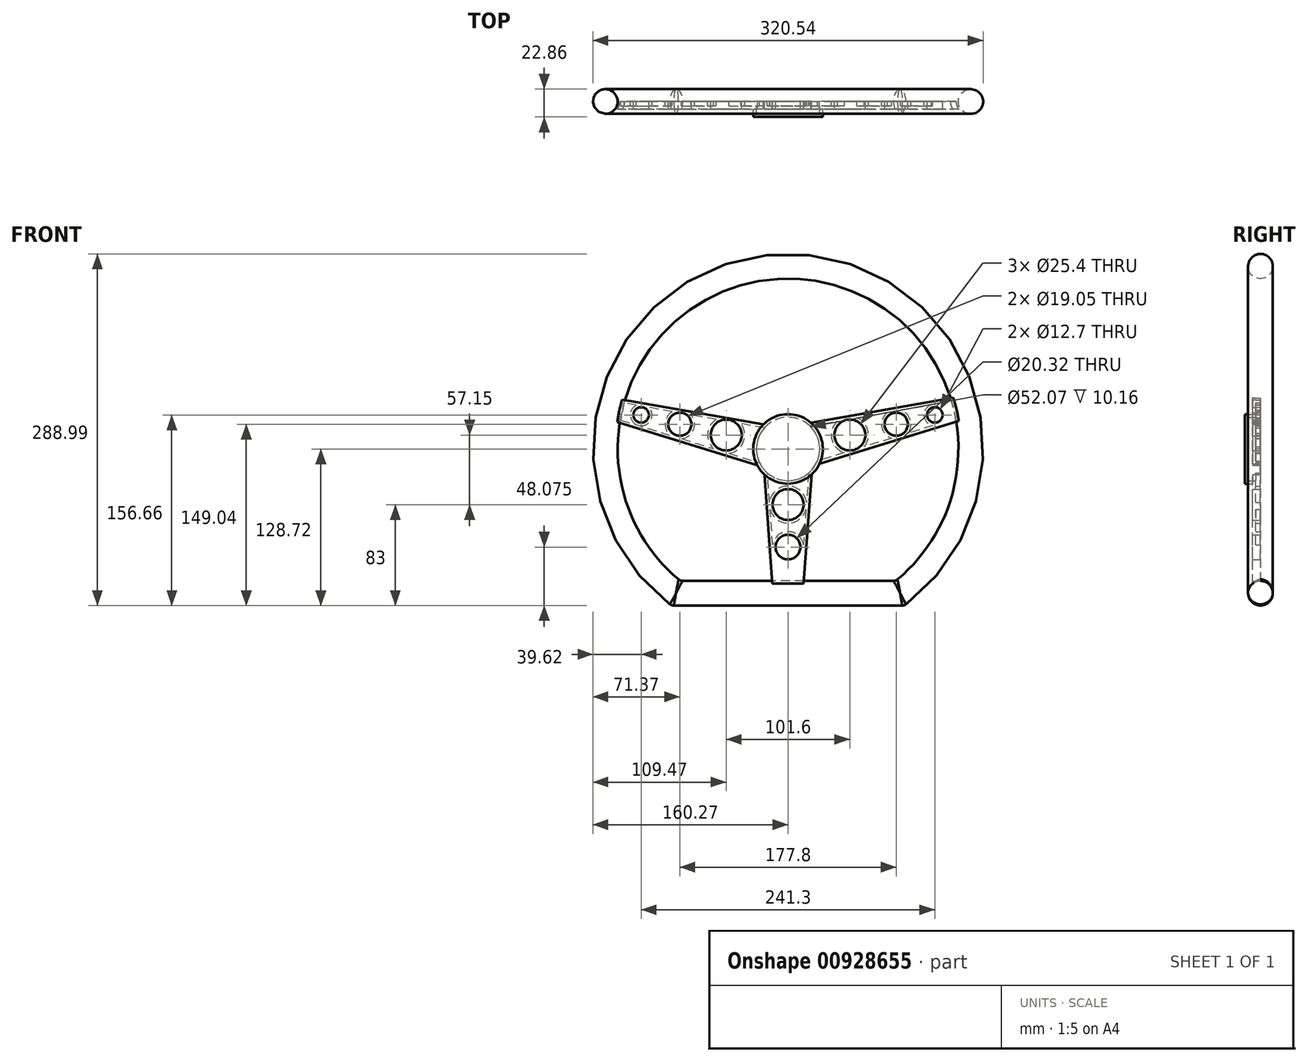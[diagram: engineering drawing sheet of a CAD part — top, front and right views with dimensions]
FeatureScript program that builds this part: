
annotation { "Feature Type Name" : "Feature", "Feature Type Description" : "" }
export const myFeature = defineFeature(function(context is Context, id is Id, definition is map)
    precondition{}
    {
        {
            var Q0;
            Q0=qCreatedBy(makeId("Front.planeOp"),FACE);
            var sketch = newSketch(context, id + "F0", { "sketchPlane" : qUnion([Q0])});
            skArc(sketch, "E0", {"start": v(92.08, -118.56) * mm, "mid": v(0, 150.11) * mm, "end": v(-92.08, -118.56) * mm});
            skLineSegment(sketch, "E1", {"start": v(-92.08, -118.56) * mm, "end": v(92.08, -118.56) * mm});
            skSolve(sketch);
        }
        {
            var Q0;
            Q0=qCreatedBy(makeId("Right.planeOp"),FACE);
            var sketch = newSketch(context, id + "F1", { "sketchPlane" : qUnion([Q0])});
            skCircle(sketch, "E2", {"center": v(0, 150.11) * mm, "radius": 10.16 * mm});
            skSolve(sketch);
        }
        {
            var Q0;
            Q0=makeQuery(id+"F1.imprint","IMPRINT",FACE,{"disambiguationData":[TD([[makeQuery(id+"F1.imprint","IMPRINT",EDGE,{"derivedFrom":sQuery(id+"F1.wireOp",EDGE,"E2")}),1.0]])]});
            var Q1;
            Q1=sQuery(id+"F0.wireOp",EDGE,"E0");
            var Q2;
            Q2=sQuery(id+"F0.wireOp",EDGE,"E1");
            sweep(context, id + "F2", {"profiles" : qUnion([Q0]), "path" : qUnion([Q1, Q2])});
        }
        {
            var Q0;
            Q0=makeQuery(id+"F2.opSweep","MID_CAP_EDGE",EDGE,{"disambiguationData":[OSD([sQuery(id+"F0.wireOp",VERTEX,"E1.end"),sQuery(id+"F1.wireOp",EDGE,"E2")]),OD(0.0)],"capPos":0.0});
            fillet(context, id + "F3", {"entities" : qUnion([Q0]), "radius" : 5.08 * mm, "tangentPropagation" : true, "allowEdgeOverflow" : false});
        }
        {
            var Q0;
            Q0=makeQuery(id+"F2.opSweep","MID_CAP_EDGE",EDGE,{"disambiguationData":[OSD([sQuery(id+"F0.wireOp",VERTEX,"E1.start"),sQuery(id+"F1.wireOp",EDGE,"E2")]),OD(0.0)],"capPos":1.0});
            fillet(context, id + "F4", {"entities" : qUnion([Q0]), "radius" : 5.08 * mm, "tangentPropagation" : true, "allowEdgeOverflow" : false});
        }
        {
            var Q0;
            Q0=makeQuery(id+"F2.opSweep","MID_CAP_EDGE",EDGE,{"disambiguationData":[OSD([sQuery(id+"F0.wireOp",VERTEX,"E1.end"),sQuery(id+"F1.wireOp",EDGE,"E2")]),OD(1.0)],"capPos":0.0});
            fillet(context, id + "F5", {"entities" : qUnion([Q0]), "radius" : 5.08 * mm, "tangentPropagation" : true, "allowEdgeOverflow" : false});
        }
        {
            var Q0;
            Q0=makeQuery(id+"F2.opSweep","MID_CAP_EDGE",EDGE,{"disambiguationData":[OSD([sQuery(id+"F0.wireOp",VERTEX,"E1.start"),sQuery(id+"F1.wireOp",EDGE,"E2")]),OD(1.0)],"capPos":1.0});
            fillet(context, id + "F6", {"entities" : qUnion([Q0]), "radius" : 5.08 * mm, "tangentPropagation" : true, "allowEdgeOverflow" : false});
        }
        {
            var Q0;
            Q0=qCreatedBy(makeId("Front.planeOp"),FACE);
            var sketch = newSketch(context, id + "F7", { "sketchPlane" : qUnion([Q0])});
            skCircle(sketch, "E3", {"center": v(0, 0) * mm, "radius": 28.58 * mm});
            skLineSegment(sketch, "E4", {"start": v(18.83, 21.49) * mm, "end": v(137.67, 42.44) * mm});
            skLineSegment(sketch, "E5", {"start": v(137.67, 42.44) * mm, "end": v(141.04, 23.36) * mm});
            skLineSegment(sketch, "E6", {"start": v(141.04, 23.36) * mm, "end": v(25.88, -12.11) * mm});
            skLineSegment(sketch, "E7", {"start": v(-20.31, 20.1) * mm, "end": v(-137.04, 40.68) * mm});
            skLineSegment(sketch, "E8", {"start": v(-137.04, 40.68) * mm, "end": v(-140.34, 21.97) * mm});
            skLineSegment(sketch, "E9", {"start": v(-140.34, 21.97) * mm, "end": v(-25.18, -13.5) * mm});
            skLineSegment(sketch, "E10", {"start": v(19.4, -20.98) * mm, "end": v(12.7, -112.18) * mm});
            skLineSegment(sketch, "E11", {"start": v(12.7, -112.18) * mm, "end": v(-12.7, -112.18) * mm});
            skLineSegment(sketch, "E12", {"start": v(-12.7, -112.18) * mm, "end": v(-19.4, -20.98) * mm});
            skCircle(sketch, "E13", {"center": v(0, -45.72) * mm, "radius": 12.7 * mm});
            skCircle(sketch, "E14", {"center": v(0, -80.65) * mm, "radius": 10.16 * mm});
            skSolve(sketch);
        }
        {
            var Q0;
            {var subQ0=sQuery(id+"F7.wireOp",EDGE,"E7");Q0=makeQuery(id+"F7.imprint","IMPRINT",FACE,{"disambiguationData":[TD([[makeQuery(id+"F7.imprint","IMPRINT",EDGE,{"derivedFrom":subQ0}),1.0]])]});}
            var Q1;
            {var subQ0=sQuery(id+"F7.wireOp",EDGE,"E4");Q1=makeQuery(id+"F7.imprint","IMPRINT",FACE,{"disambiguationData":[TD([[makeQuery(id+"F7.imprint","IMPRINT",EDGE,{"derivedFrom":subQ0}),-1.0]])]});}
            var Q2;
            {var subQ0=sQuery(id+"F7.wireOp",EDGE,"E10");Q2=makeQuery(id+"F7.imprint","IMPRINT",FACE,{"disambiguationData":[TD([[makeQuery(id+"F7.imprint","IMPRINT",EDGE,{"derivedFrom":subQ0}),-1.0]])]});}
            var Q3;
            {var subQ0=sQuery(id+"F7.wireOp",EDGE,"E12");Q3=makeQuery(id+"F7.imprint","IMPRINT",FACE,{"disambiguationData":[TD([[makeQuery(id+"F7.imprint","IMPRINT",EDGE,{"derivedFrom":subQ0}),-1.0]])]});}
            extrude(context, id + "F8", {"entities" : qUnion([Q0, Q1, Q2, Q3]), "operationType" : NewBodyOperationType.ADD, "depth" : 6.35 * mm, "offsetDistance" : 25.4 * mm});
        }
        {
            var Q0;
            {var subQ0=sQuery(id+"F7.wireOp",EDGE,"E3");var subQ5=makeQuery(id+"F7.imprint","INTERSECT",VERTEX,{"derivedFrom":[subQ0,sQuery(id+"F7.wireOp",EDGE,"E4")]});Q0=makeQuery(id+"F7.imprint","IMPRINT",FACE,{"disambiguationData":[TD([[makeQuery(id+"F7.imprint","IMPRINT",EDGE,{"disambiguationData":[TD([[subQ5,-1.0]])],"derivedFrom":subQ0}),1.0]])]});}
            extrude(context, id + "F9", {"entities" : qUnion([Q0]), "operationType" : NewBodyOperationType.ADD, "depth" : 12.7 * mm, "offsetDistance" : 25.4 * mm});
        }
        {
            var Q0;
            Q0=qCreatedBy(makeId("Front.planeOp"),FACE);
            var sketch = newSketch(context, id + "F10", { "sketchPlane" : qUnion([Q0])});
            skCircle(sketch, "E15", {"center": v(-50.8, 11.43) * mm, "radius": 12.7 * mm});
            skCircle(sketch, "E16", {"center": v(50.8, 11.43) * mm, "radius": 12.7 * mm});
            skCircle(sketch, "E17", {"center": v(-88.9, 20.32) * mm, "radius": 9.53 * mm});
            skCircle(sketch, "E18", {"center": v(88.9, 20.32) * mm, "radius": 9.53 * mm});
            skCircle(sketch, "E19", {"center": v(120.65, 27.94) * mm, "radius": 6.35 * mm});
            skCircle(sketch, "E20", {"center": v(-120.65, 27.94) * mm, "radius": 6.35 * mm});
            skSolve(sketch);
        }
        {
            var Q0;
            Q0 = qSketchRegion(id + "F10", true);
            extrude(context, id + "F11", {"entities" : qUnion([Q0]), "operationType" : NewBodyOperationType.REMOVE, "depth" : 25.4 * mm, "offsetDistance" : 25.4 * mm});
        }
        {
            var Q0;
            {var subQ0=sQuery(id+"F7.wireOp",EDGE,"E3");Q0=makeQuery(id+"F9.boolean.opBoolean","MERGE",FACE,{"derivedFrom":[makeQuery(id+"F8.opExtrude","CAP_FACE",FACE,{"disambiguationData":[OSD([subQ0,sQuery(id+"F7.wireOp",EDGE,"E7"),sQuery(id+"F7.wireOp",EDGE,"E8"),sQuery(id+"F7.wireOp",EDGE,"E9")])],"isStart":true}),makeQuery(id+"F8.opExtrude","CAP_FACE",FACE,{"disambiguationData":[OSD([subQ0,sQuery(id+"F7.wireOp",EDGE,"E10"),sQuery(id+"F7.wireOp",EDGE,"E11"),sQuery(id+"F7.wireOp",EDGE,"E12"),sQuery(id+"F7.wireOp",EDGE,"E13"),sQuery(id+"F7.wireOp",EDGE,"E14")])],"isStart":true}),makeQuery(id+"F8.opExtrude","CAP_FACE",FACE,{"disambiguationData":[OSD([subQ0,sQuery(id+"F7.wireOp",EDGE,"E4"),sQuery(id+"F7.wireOp",EDGE,"E5"),sQuery(id+"F7.wireOp",EDGE,"E6")])],"isStart":true}),makeQuery(id+"F9.opExtrude","CAP_FACE",FACE,{"disambiguationData":[OSD([subQ0])],"isStart":true})]});}
            shell(context, id + "F12", {"entities" : qUnion([Q0]), "thickness" : 2.54 * mm});
        }
    });
